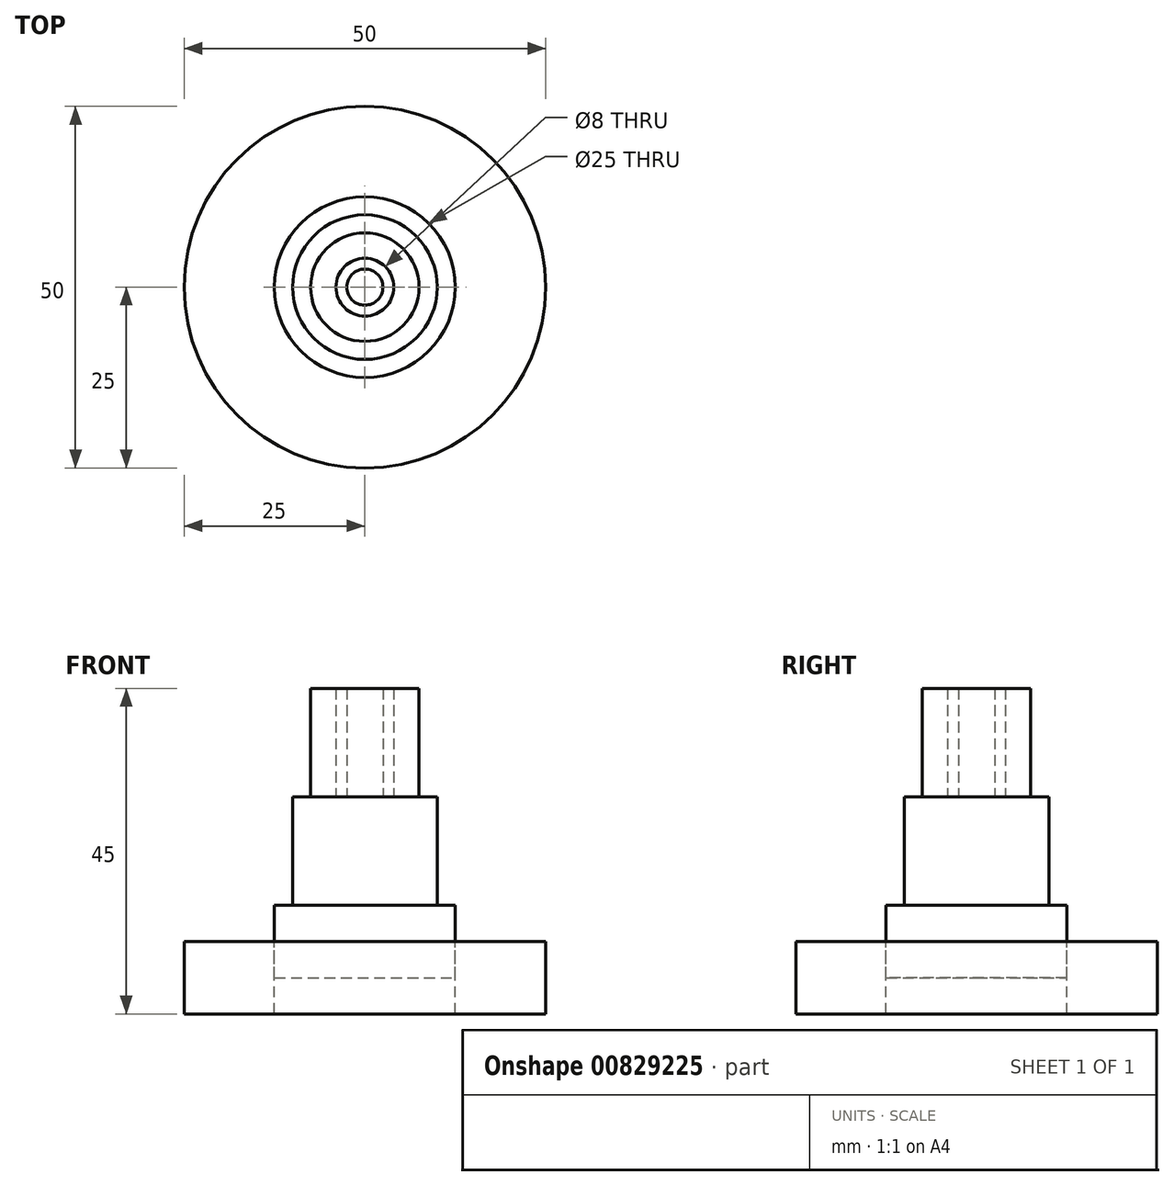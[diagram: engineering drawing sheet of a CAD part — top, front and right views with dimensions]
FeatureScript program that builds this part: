
annotation { "Feature Type Name" : "Feature", "Feature Type Description" : "" }
export const myFeature = defineFeature(function(context is Context, id is Id, definition is map)
    precondition{}
    {
        {
            var Q0;
            Q0=qCreatedBy(makeId("Top.planeOp"),FACE);
            var sketch = newSketch(context, id + "F0", { "sketchPlane" : qUnion([Q0])});
            skCircle(sketch, "E0", {"center": v(0, 0) * mm, "radius": 2.5 * mm});
            skCircle(sketch, "E1", {"center": v(0, 0) * mm, "radius": 4 * mm});
            skCircle(sketch, "E2", {"center": v(0, 0) * mm, "radius": 7.5 * mm});
            skSolve(sketch);
        }
        {
            var Q0;
            Q0=makeQuery(id+"F0.imprint","IMPRINT",FACE,{"disambiguationData":[TD([[makeQuery(id+"F0.imprint","IMPRINT",EDGE,{"derivedFrom":sQuery(id+"F0.wireOp",EDGE,"E1")}),-1.0]])]});
            var Q1;
            Q1=makeQuery(id+"F0.imprint","IMPRINT",FACE,{"disambiguationData":[TD([[makeQuery(id+"F0.imprint","IMPRINT",EDGE,{"derivedFrom":sQuery(id+"F0.wireOp",EDGE,"E0")}),1.0]])]});
            extrude(context, id + "F1", {"entities" : qUnion([Q0, Q1]), "depth" : 15 * mm, "offsetDistance" : 25 * mm});
        }
        {
            var Q0;
            Q0=qCreatedBy(makeId("Top.planeOp"),FACE);
            var sketch = newSketch(context, id + "F2", { "sketchPlane" : qUnion([Q0])});
            skCircle(sketch, "E3", {"center": v(0, 0) * mm, "radius": 10 * mm});
            skSolve(sketch);
        }
        {
            var Q0;
            Q0=makeQuery(id+"F2.imprint","IMPRINT",FACE,{"disambiguationData":[TD([[makeQuery(id+"F2.imprint","IMPRINT",EDGE,{"derivedFrom":sQuery(id+"F2.wireOp",EDGE,"E3")}),1.0]])]});
            extrude(context, id + "F3", {"entities" : qUnion([Q0]), "depth" : -15 * mm, "offsetDistance" : 25 * mm});
        }
        {
            var Q0;
            Q0=makeQuery(id+"F3.opExtrude","CAP_FACE",FACE,{"disambiguationData":[OSD([sQuery(id+"F2.wireOp",EDGE,"E3")])],"isStart":false});
            var sketch = newSketch(context, id + "F4", { "sketchPlane" : qUnion([Q0])});
            skCircle(sketch, "E4", {"center": v(0, 0) * mm, "radius": 12.5 * mm});
            skSolve(sketch);
        }
        {
            var Q0;
            Q0 = qSketchRegion(id + "F4", true);
            extrude(context, id + "F5", {"entities" : qUnion([Q0]), "operationType" : NewBodyOperationType.ADD, "depth" : 5 * mm, "offsetDistance" : 25 * mm});
        }
        {
            var Q0;
            Q0=makeQuery(id+"F5.opExtrude","CAP_FACE",FACE,{"disambiguationData":[OSD([sQuery(id+"F4.wireOp",EDGE,"E4")])],"isStart":false});
            var sketch = newSketch(context, id + "F6", { "sketchPlane" : qUnion([Q0])});
            skCircle(sketch, "E5", {"center": v(0, 0) * mm, "radius": 12.5 * mm});
            skSolve(sketch);
        }
        {
            var Q0;
            Q0=makeQuery(id+"F6.imprint","IMPRINT",FACE,{"disambiguationData":[TD([[makeQuery(id+"F6.imprint","IMPRINT",EDGE,{"derivedFrom":sQuery(id+"F6.wireOp",EDGE,"E5")}),1.0]])]});
            var sketch = newSketch(context, id + "F7", { "sketchPlane" : qUnion([Q0])});
            skCircle(sketch, "E6", {"center": v(0, 0) * mm, "radius": 25 * mm});
            skSolve(sketch);
        }
        {
            var Q0;
            Q0=makeQuery(id+"F7.imprint","IMPRINT",FACE,{"disambiguationData":[TD([[makeQuery(id+"F7.imprint","IMPRINT",EDGE,{"derivedFrom":sQuery(id+"F7.wireOp",EDGE,"E6")}),1.0]])]});
            extrude(context, id + "F8", {"entities" : qUnion([Q0]), "operationType" : NewBodyOperationType.ADD, "depth" : 10 * mm, "offsetDistance" : 25 * mm});
        }
        {
            var Q0;
            Q0=makeQuery(id+"F6.imprint","IMPRINT",FACE,{"disambiguationData":[TD([[makeQuery(id+"F6.imprint","IMPRINT",EDGE,{"derivedFrom":sQuery(id+"F6.wireOp",EDGE,"E5")}),1.0]])]});
            extrude(context, id + "F9", {"entities" : qUnion([Q0]), "depth" : 5 * mm, "offsetDistance" : 25 * mm});
        }
    });
